# Revit family: L-one 5x2
name_source: partatom
category: Осветительные приборы
revit_build: Autodesk Revit 2017 (Build: 20160225_1515(x64)
units: mm (PartAtom-declared; Revit-internal decimal feet)

## family parameters
Источник света = Да
Общий = Нет
Основа = Грань
При загрузке вырезать с полостями = Нет
Размер круглого соединителя = Использовать диаметр
Тип детали = Нормальный
Точка расчета площади = Нет

## types (2) — shared parameters
Видимая форма излучения при визуализации = Нет
Изготовитель = LEDEL
Излучение по длине прямоугольника = 79 мм
Излучение по ширине прямоугольника = 138 мм
Комментарии к типоразмеру = Бытовые
Отметка по умолчанию = 1219 мм
Полная установленная мощность = 10 В·А
Светофильтр = 16777215
Смещение цветовой температуры при затухании лампы = <Нет>
Угол наклона = 90.00°

## per-type parameters (varying)
| type | Артикул | Файл фотометрической сетки |
| L-One-5x2-10-D-5.0K | 501003 | L-one 5x2-10-Д-5.0K-02.ies |
| L-One-5x2-10-D-3.0K | 501001 | L-one 5x2-10-Д-3.0K-02.ies |

## geometry (parser evidence)
native form markers: Sweep x2
no freeform markers — native parametric forms only
